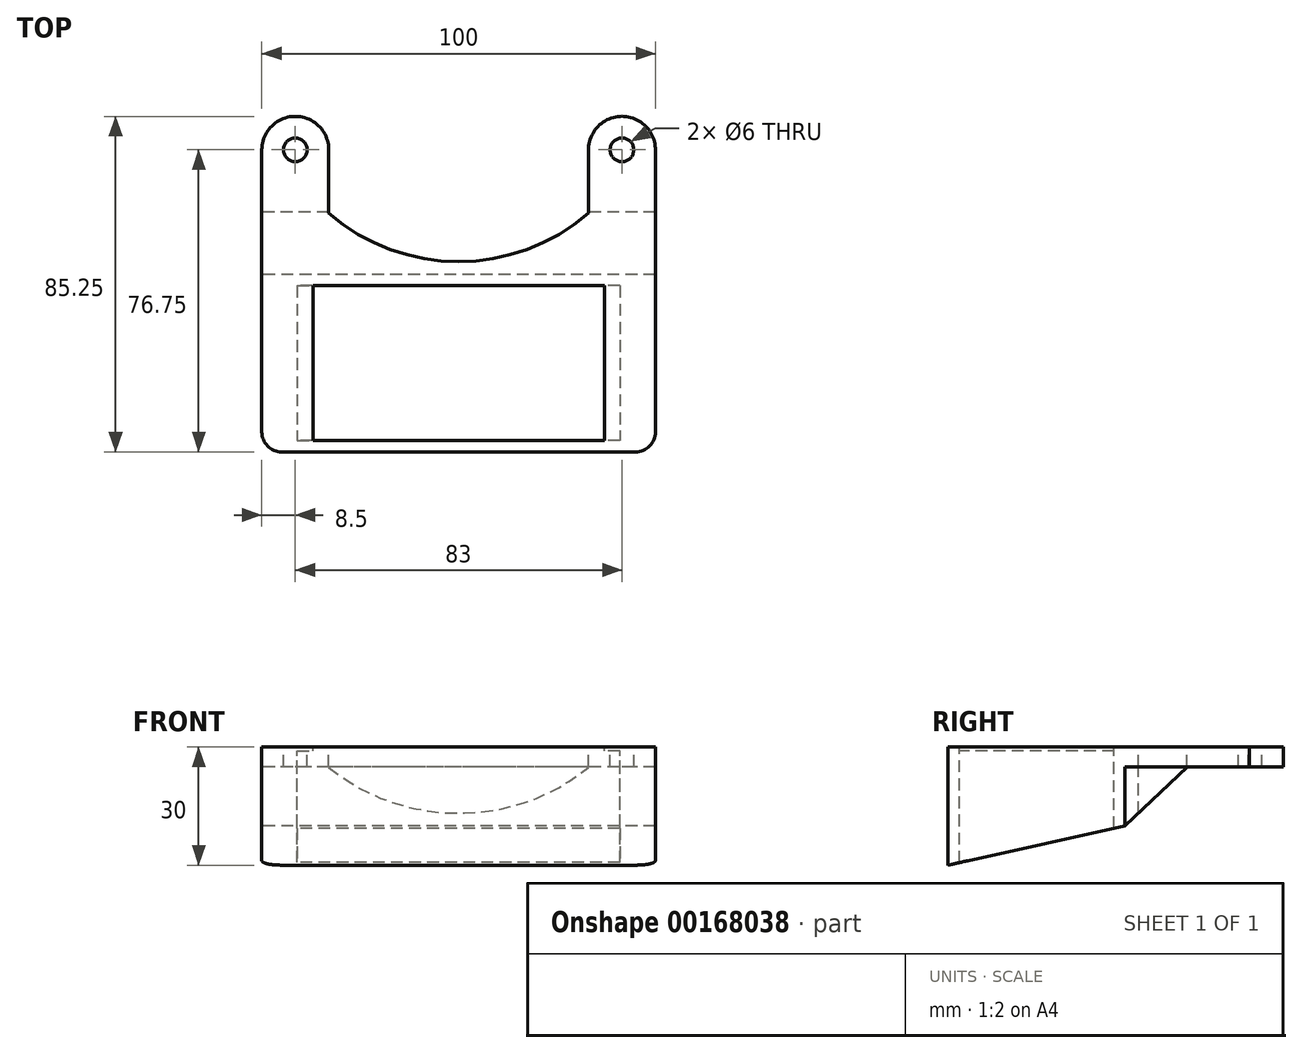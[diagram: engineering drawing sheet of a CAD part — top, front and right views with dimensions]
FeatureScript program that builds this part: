
annotation { "Feature Type Name" : "Feature", "Feature Type Description" : "" }
export const myFeature = defineFeature(function(context is Context, id is Id, definition is map)
    precondition{}
    {
        {
            var Q0;
            Q0=qCreatedBy(makeId("Top.planeOp"),FACE);
            var sketch = newSketch(context, id + "F0", { "sketchPlane" : qUnion([Q0])});
            skLineSegment(sketch, "E0.bottom", {"start": v(0, 0) * mm, "end": v(100, 0) * mm});
            skLineSegment(sketch, "E0.top", {"start": v(0, 45) * mm, "end": v(100, 45) * mm});
            skLineSegment(sketch, "E0.left", {"start": v(0, 0) * mm, "end": v(0, 45) * mm});
            skLineSegment(sketch, "E0.right", {"start": v(100, 0) * mm, "end": v(100, 45) * mm});
            skSolve(sketch);
        }
        {
            var Q0;
            Q0 = qSketchRegion(id + "F0", true);
            extrude(context, id + "F1", {"entities" : qUnion([Q0]), "depth" : 30 * mm});
        }
        {
            var Q0;
            Q0=makeQuery(id+"F1.opExtrude","CAP_FACE",FACE,{"disambiguationData":[OSD([sQuery(id+"F0.wireOp",EDGE,"E0.bottom"),sQuery(id+"F0.wireOp",EDGE,"E0.top"),sQuery(id+"F0.wireOp",EDGE,"E0.left"),sQuery(id+"F0.wireOp",EDGE,"E0.right")])],"isStart":false});
            var sketch = newSketch(context, id + "F2", { "sketchPlane" : qUnion([Q0])});
            skLineSegment(sketch, "E1.bottom", {"start": v(13, 2.9) * mm, "end": v(87, 2.9) * mm});
            skLineSegment(sketch, "E1.top", {"start": v(13, 42.2) * mm, "end": v(87, 42.2) * mm});
            skLineSegment(sketch, "E1.left", {"start": v(13, 2.9) * mm, "end": v(13, 42.2) * mm});
            skLineSegment(sketch, "E1.right", {"start": v(87, 2.9) * mm, "end": v(87, 42.2) * mm});
            skSolve(sketch);
        }
        {
            var Q0;
            Q0 = qSketchRegion(id + "F2", true);
            extrude(context, id + "F3", {"entities" : qUnion([Q0]), "operationType" : NewBodyOperationType.REMOVE, "endBound" : BoundingType.THROUGH_ALL, "oppositeDirection" : true, "depth" : 25.4 * mm});
        }
        {
            var Q0;
            Q0=makeQuery(id+"F1.opExtrude","SWEPT_FACE",FACE,{"disambiguationData":[OSD([sQuery(id+"F0.wireOp",EDGE,"E0.left")])]});
            var sketch = newSketch(context, id + "F4", { "sketchPlane" : qUnion([Q0])});
            skLineSegment(sketch, "E2", {"start": v(0, 0) * mm, "end": v(-45, 10) * mm});
            skLineSegment(sketch, "E3", {"start": v(-45, 10) * mm, "end": v(-45, 0) * mm});
            skLineSegment(sketch, "E4", {"start": v(-45, 0) * mm, "end": v(0, 0) * mm});
            skSolve(sketch);
        }
        {
            var Q0;
            Q0 = qSketchRegion(id + "F4", true);
            extrude(context, id + "F5", {"entities" : qUnion([Q0]), "operationType" : NewBodyOperationType.REMOVE, "endBound" : BoundingType.THROUGH_ALL, "oppositeDirection" : true, "depth" : 25.4 * mm});
        }
        {
            var Q0;
            Q0=makeQuery(id+"F1.opExtrude","CAP_FACE",FACE,{"disambiguationData":[OSD([sQuery(id+"F0.wireOp",EDGE,"E0.bottom"),sQuery(id+"F0.wireOp",EDGE,"E0.top"),sQuery(id+"F0.wireOp",EDGE,"E0.left"),sQuery(id+"F0.wireOp",EDGE,"E0.right")])],"isStart":false});
            var sketch = newSketch(context, id + "F6", { "sketchPlane" : qUnion([Q0])});
            skArc(sketch, "E5", {"start": v(16.99, 76.31) * mm, "mid": v(8.72, 85.25) * mm, "end": v(0, 76.75) * mm});
            skArc(sketch, "E6", {"start": v(100, 76.59) * mm, "mid": v(91.51, 85.25) * mm, "end": v(83, 76.6) * mm});
            skLineSegment(sketch, "E7", {"start": v(0, 76.75) * mm, "end": v(0, 45) * mm});
            skLineSegment(sketch, "E8", {"start": v(16.99, 76.31) * mm, "end": v(16.99, 60.66) * mm});
            skLineSegment(sketch, "E9", {"start": v(83, 76.6) * mm, "end": v(83, 60.66) * mm});
            skLineSegment(sketch, "E10", {"start": v(100, 76.59) * mm, "end": v(100, 45) * mm});
            skLineSegment(sketch, "E11", {"start": v(16.99, 60.66) * mm, "end": v(83, 60.66) * mm});
            skPoint(sketch, "E12.orphan", {"position": v(16.99, 45) * mm});
            skLineSegment(sketch, "E13", {"start": v(0, 45) * mm, "end": v(100, 45) * mm});
            skSolve(sketch);
        }
        {
            var Q0;
            Q0 = qSketchRegion(id + "F6", true);
            extrude(context, id + "F7", {"entities" : qUnion([Q0]), "oppositeDirection" : true, "depth" : 5 * mm});
        }
        {
            var Q0;
            Q0=makeQuery(id+"F7.opExtrude","SWEPT_BODY",BODY,{"disambiguationData":[OSD([sQuery(id+"F6.wireOp",EDGE,"E5"),sQuery(id+"F6.wireOp",EDGE,"E6"),sQuery(id+"F6.wireOp",EDGE,"E7"),sQuery(id+"F6.wireOp",EDGE,"E8"),sQuery(id+"F6.wireOp",EDGE,"E9"),sQuery(id+"F6.wireOp",EDGE,"E10"),sQuery(id+"F6.wireOp",EDGE,"E11"),sQuery(id+"F6.wireOp",EDGE,"E13")])]});
            var Q1;
            Q1=makeQuery(id+"F1.opExtrude","SWEPT_BODY",BODY,{"disambiguationData":[OSD([sQuery(id+"F0.wireOp",EDGE,"E0.bottom"),sQuery(id+"F0.wireOp",EDGE,"E0.top"),sQuery(id+"F0.wireOp",EDGE,"E0.left"),sQuery(id+"F0.wireOp",EDGE,"E0.right")])]});
            booleanBodies(context, id + "F8", {"operationType" : BooleanOperationType.UNION, "tools" : qUnion([Q0, Q1])});
        }
        {
            var Q0;
            Q0=makeQuery(id+"F8.opBoolean","MERGE",FACE,{"derivedFrom":[makeQuery(id+"F1.opExtrude","SWEPT_FACE",FACE,{"disambiguationData":[OSD([sQuery(id+"F0.wireOp",EDGE,"E0.left")])]}),makeQuery(id+"F7.opExtrude","SWEPT_FACE",FACE,{"disambiguationData":[OSD([sQuery(id+"F6.wireOp",EDGE,"E7")])]})]});
            var sketch = newSketch(context, id + "F9", { "sketchPlane" : qUnion([Q0])});
            skLineSegment(sketch, "E14", {"start": v(-45, 10) * mm, "end": v(-60.88, 25) * mm});
            skLineSegment(sketch, "E15", {"start": v(-60.88, 25) * mm, "end": v(-45, 25) * mm});
            skLineSegment(sketch, "E16", {"start": v(-45, 25) * mm, "end": v(-45, 10) * mm});
            skSolve(sketch);
        }
        {
            var Q0;
            Q0 = qSketchRegion(id + "F9", true);
            extrude(context, id + "F10", {"entities" : qUnion([Q0]), "oppositeDirection" : true, "depth" : 100 * mm});
        }
        {
            var Q0;
            Q0=makeQuery(id+"F8.opBoolean","MERGE",FACE,{"derivedFrom":[makeQuery(id+"F1.opExtrude","CAP_FACE",FACE,{"disambiguationData":[OSD([sQuery(id+"F0.wireOp",EDGE,"E0.bottom"),sQuery(id+"F0.wireOp",EDGE,"E0.top"),sQuery(id+"F0.wireOp",EDGE,"E0.left"),sQuery(id+"F0.wireOp",EDGE,"E0.right")])],"isStart":false}),makeQuery(id+"F7.opExtrude","CAP_FACE",FACE,{"disambiguationData":[OSD([sQuery(id+"F6.wireOp",EDGE,"E5"),sQuery(id+"F6.wireOp",EDGE,"E6"),sQuery(id+"F6.wireOp",EDGE,"E7"),sQuery(id+"F6.wireOp",EDGE,"E8"),sQuery(id+"F6.wireOp",EDGE,"E9"),sQuery(id+"F6.wireOp",EDGE,"E10"),sQuery(id+"F6.wireOp",EDGE,"E11"),sQuery(id+"F6.wireOp",EDGE,"E13")])],"isStart":true})]});
            var sketch = newSketch(context, id + "F11", { "sketchPlane" : qUnion([Q0])});
            skArc(sketch, "E17", {"start": v(16.99, 60.66) * mm, "mid": v(50, 48.35) * mm, "end": v(83, 60.66) * mm});
            skPoint(sketch, "E17.centerSnap0", {"position": v(50, 60.66) * mm});
            skLineSegment(sketch, "E18", {"start": v(16.99, 65.04) * mm, "end": v(83, 65.04) * mm});
            skLineSegment(sketch, "E19", {"start": v(83, 65.04) * mm, "end": v(83, 60.66) * mm});
            skLineSegment(sketch, "E20", {"start": v(16.99, 65.04) * mm, "end": v(16.99, 60.66) * mm});
            skSolve(sketch);
        }
        {
            var Q0;
            Q0 = qSketchRegion(id + "F11", true);
            extrude(context, id + "F12", {"entities" : qUnion([Q0]), "operationType" : NewBodyOperationType.REMOVE, "oppositeDirection" : true, "depth" : 25.4 * mm});
        }
        {
            var Q0;
            Q0=makeQuery(id+"F8.opBoolean","MERGE",FACE,{"derivedFrom":[makeQuery(id+"F1.opExtrude","CAP_FACE",FACE,{"disambiguationData":[OSD([sQuery(id+"F0.wireOp",EDGE,"E0.bottom"),sQuery(id+"F0.wireOp",EDGE,"E0.top"),sQuery(id+"F0.wireOp",EDGE,"E0.left"),sQuery(id+"F0.wireOp",EDGE,"E0.right")])],"isStart":false}),makeQuery(id+"F7.opExtrude","CAP_FACE",FACE,{"disambiguationData":[OSD([sQuery(id+"F6.wireOp",EDGE,"E5"),sQuery(id+"F6.wireOp",EDGE,"E6"),sQuery(id+"F6.wireOp",EDGE,"E7"),sQuery(id+"F6.wireOp",EDGE,"E8"),sQuery(id+"F6.wireOp",EDGE,"E9"),sQuery(id+"F6.wireOp",EDGE,"E10"),sQuery(id+"F6.wireOp",EDGE,"E11"),sQuery(id+"F6.wireOp",EDGE,"E13")])],"isStart":true})]});
            var sketch = newSketch(context, id + "F13", { "sketchPlane" : qUnion([Q0])});
            skCircle(sketch, "E21", {"center": v(8.5, 76.75) * mm, "radius": 3 * mm});
            skCircle(sketch, "E22", {"center": v(91.5, 76.75) * mm, "radius": 3 * mm});
            skSolve(sketch);
        }
        {
            var Q0;
            Q0 = qSketchRegion(id + "F13", true);
            extrude(context, id + "F14", {"entities" : qUnion([Q0]), "operationType" : NewBodyOperationType.REMOVE, "oppositeDirection" : true, "depth" : 25.4 * mm});
        }
        {
            var Q0;
            Q0=makeQuery(id+"F1.opExtrude","SWEPT_EDGE",EDGE,{"disambiguationData":[OSD([sQuery(id+"F0.wireOp",EDGE,"E0.bottom"),sQuery(id+"F0.wireOp",EDGE,"E0.left")])]});
            var Q1;
            Q1=makeQuery(id+"F1.opExtrude","SWEPT_EDGE",EDGE,{"disambiguationData":[OSD([sQuery(id+"F0.wireOp",EDGE,"E0.bottom"),sQuery(id+"F0.wireOp",EDGE,"E0.right")])]});
            fillet(context, id + "F15", {"entities" : qUnion([Q0, Q1]), "radius" : 5.08 * mm, "tangentPropagation" : true, "allowEdgeOverflow" : false});
        }
        {
            var Q0;
            Q0=makeQuery(id+"F3.boolean.opBoolean","COPY",FACE,{"derivedFrom":makeQuery(id+"F3.opExtrude","SWEPT_FACE",FACE,{"disambiguationData":[OSD([sQuery(id+"F2.wireOp",EDGE,"E1.left")])]})});
            var sketch = newSketch(context, id + "F16", { "sketchPlane" : qUnion([Q0])});
            skLineSegment(sketch, "E23", {"start": v(2.9, 0.64) * mm, "end": v(42.2, 9.38) * mm});
            skLineSegment(sketch, "E24", {"start": v(42.2, 9.38) * mm, "end": v(42.2, 29) * mm});
            skLineSegment(sketch, "E25", {"start": v(42.2, 29) * mm, "end": v(2.9, 29) * mm});
            skLineSegment(sketch, "E26", {"start": v(2.9, 29) * mm, "end": v(2.9, 0.64) * mm});
            skSolve(sketch);
        }
        {
            var Q0;
            Q0 = qSketchRegion(id + "F16", true);
            extrude(context, id + "F17", {"entities" : qUnion([Q0]), "operationType" : NewBodyOperationType.REMOVE, "oppositeDirection" : true, "depth" : 4 * mm});
        }
        {
            var Q0;
            Q0=makeQuery(id+"F3.boolean.opBoolean","COPY",FACE,{"derivedFrom":makeQuery(id+"F3.opExtrude","SWEPT_FACE",FACE,{"disambiguationData":[OSD([sQuery(id+"F2.wireOp",EDGE,"E1.right")])]})});
            var sketch = newSketch(context, id + "F18", { "sketchPlane" : qUnion([Q0])});
            skLineSegment(sketch, "E27", {"start": v(-2.9, 0.64) * mm, "end": v(-42.2, 9.38) * mm});
            skLineSegment(sketch, "E28", {"start": v(-42.2, 9.38) * mm, "end": v(-42.2, 29) * mm});
            skLineSegment(sketch, "E29", {"start": v(-42.2, 29) * mm, "end": v(-2.9, 29) * mm});
            skLineSegment(sketch, "E30", {"start": v(-2.9, 29) * mm, "end": v(-2.9, 0.64) * mm});
            skSolve(sketch);
        }
        {
            var Q0;
            Q0 = qSketchRegion(id + "F18", true);
            extrude(context, id + "F19", {"entities" : qUnion([Q0]), "operationType" : NewBodyOperationType.REMOVE, "oppositeDirection" : true, "depth" : 4 * mm});
        }
    });
